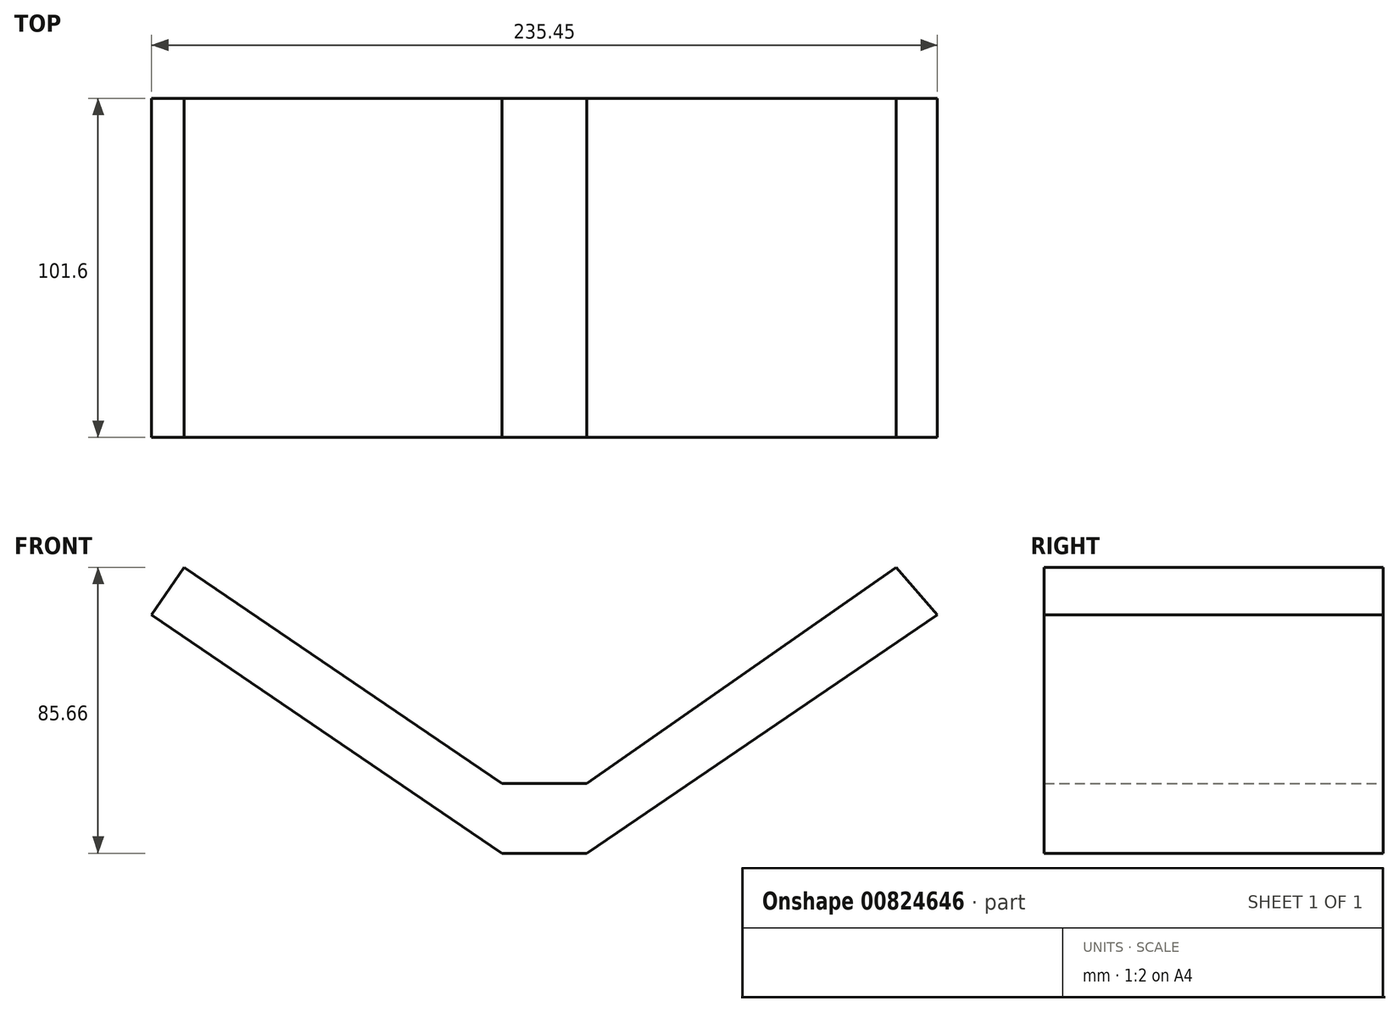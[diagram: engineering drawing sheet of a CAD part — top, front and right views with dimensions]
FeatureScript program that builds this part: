
annotation { "Feature Type Name" : "Feature", "Feature Type Description" : "" }
export const myFeature = defineFeature(function(context is Context, id is Id, definition is map)
    precondition{}
    {
        {
            var Q0;
            Q0=qCreatedBy(makeId("Front.planeOp"),FACE);
            var sketch = newSketch(context, id + "F0", { "sketchPlane" : qUnion([Q0])});
            skLineSegment(sketch, "E0", {"start": v(5.05, -71.4) * mm, "end": v(-20.35, -71.4) * mm});
            skLineSegment(sketch, "E1", {"start": v(-20.35, -71.4) * mm, "end": v(-125.37, 0) * mm});
            skLineSegment(sketch, "E2", {"start": v(5.05, -71.4) * mm, "end": v(110.08, 0) * mm});
            skLineSegment(sketch, "E3", {"start": v(-125.37, 0) * mm, "end": v(-115.68, 14.25) * mm});
            skLineSegment(sketch, "E4", {"start": v(-115.68, 14.25) * mm, "end": v(-20.35, -50.56) * mm});
            skLineSegment(sketch, "E5", {"start": v(-20.35, -50.56) * mm, "end": v(5.05, -50.56) * mm});
            skLineSegment(sketch, "E6", {"start": v(5.05, -50.56) * mm, "end": v(97.71, 14.25) * mm});
            skLineSegment(sketch, "E7", {"start": v(97.71, 14.25) * mm, "end": v(110.08, 0) * mm});
            skSolve(sketch);
        }
        {
            var Q0;
            Q0=makeQuery(id+"F0.imprint","IMPRINT",FACE,{"disambiguationData":[TD([[makeQuery(id+"F0.imprint","IMPRINT",EDGE,{"derivedFrom":sQuery(id+"F0.wireOp",EDGE,"E0")}),-1.0]])]});
            extrude(context, id + "F1", {"entities" : qUnion([Q0]), "depth" : 101.6 * mm, "offsetDistance" : 25.4 * mm});
        }
    });
